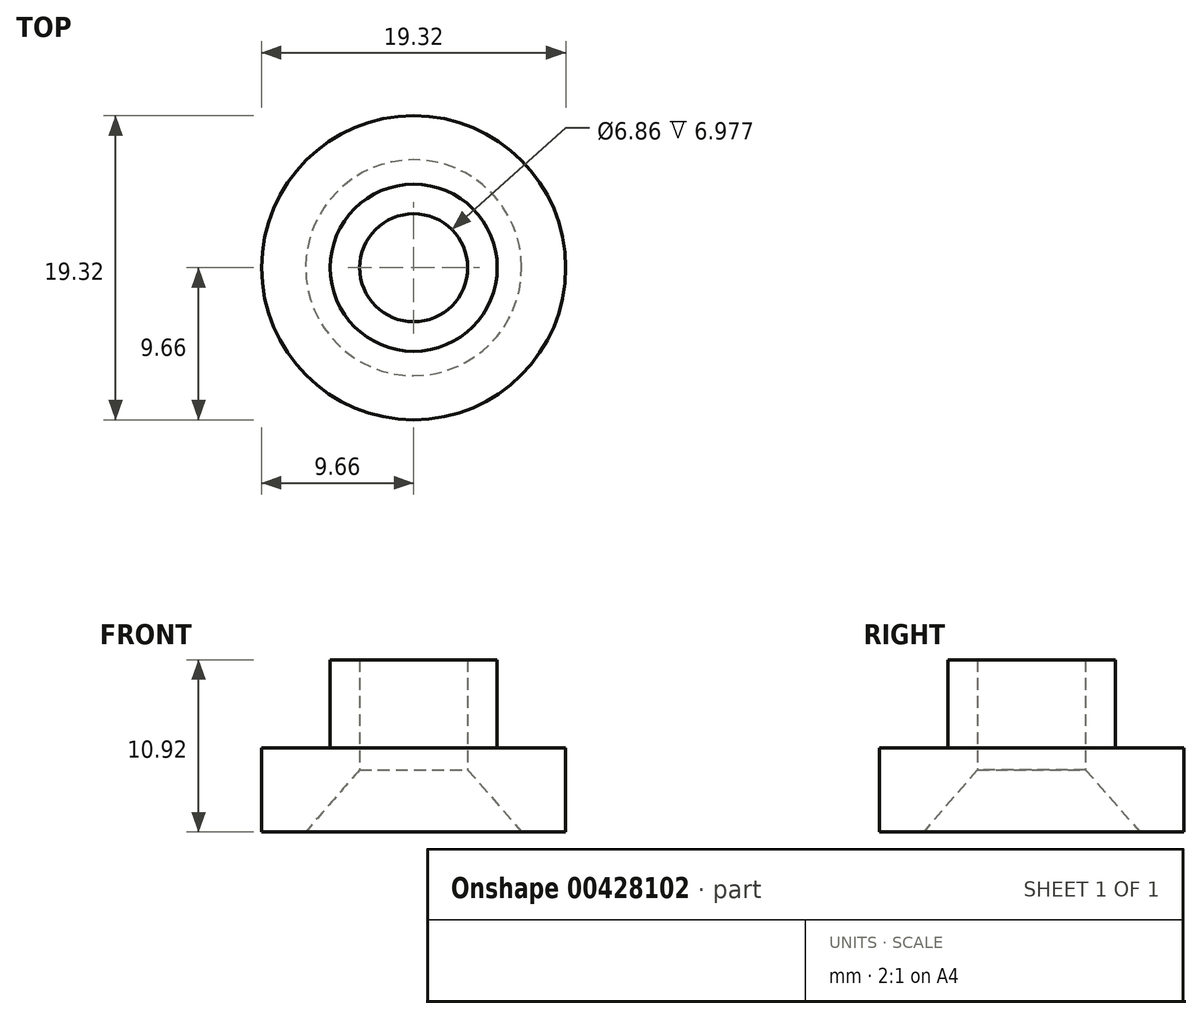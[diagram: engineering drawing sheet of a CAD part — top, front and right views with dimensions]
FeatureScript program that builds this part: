
annotation { "Feature Type Name" : "Feature", "Feature Type Description" : "" }
export const myFeature = defineFeature(function(context is Context, id is Id, definition is map)
    precondition{}
    {
        {
            var Q0;
            Q0=qCreatedBy(makeId("Top.planeOp"),FACE);
            var sketch = newSketch(context, id + "F0", { "sketchPlane" : qUnion([Q0])});
            skCircle(sketch, "E0", {"center": v(0, 0) * mm, "radius": 9.66 * mm});
            skSolve(sketch);
        }
        {
            var Q0;
            Q0=makeQuery(id+"F0.imprint","IMPRINT",FACE,{"disambiguationData":[TD([[makeQuery(id+"F0.imprint","IMPRINT",EDGE,{"derivedFrom":sQuery(id+"F0.wireOp",EDGE,"E0")}),1.0]])]});
            var Q1;
            Q1=sQuery(id+"F0.wireOp",EDGE,"E0");
            extrude(context, id + "F1", {"entities" : qUnion([Q0]), "surfaceEntities" : qUnion([Q1]), "depth" : 5.33 * mm});
        }
        {
            var Q0;
            Q0=makeQuery(id+"F1.opExtrude","CAP_FACE",FACE,{"disambiguationData":[OSD([sQuery(id+"F0.wireOp",EDGE,"E0")])],"isStart":false});
            var sketch = newSketch(context, id + "F2", { "sketchPlane" : qUnion([Q0])});
            skCircle(sketch, "E1", {"center": v(0, 0) * mm, "radius": 5.3 * mm});
            skSolve(sketch);
        }
        {
            var Q0;
            Q0 = qSketchRegion(id + "F2", true);
            extrude(context, id + "F3", {"entities" : qUnion([Q0]), "operationType" : NewBodyOperationType.ADD, "depth" : 5.6 * mm});
        }
        {
            var Q0;
            Q0=makeQuery(id+"F1.opExtrude","CAP_FACE",FACE,{"disambiguationData":[OSD([sQuery(id+"F0.wireOp",EDGE,"E0")])],"isStart":true});
            var sketch = newSketch(context, id + "F4", { "sketchPlane" : qUnion([Q0])});
            skPoint(sketch, "E2", {"position": v(0, 0) * mm});
            skSolve(sketch);
        }
        {
            var Q0;
            Q0=sQuery(id+"F4.wireOp",VERTEX,"E2");
            var Q1;
            Q1=makeQuery(id+"F1.opExtrude","SWEPT_BODY",BODY,{"disambiguationData":[OSD([sQuery(id+"F0.wireOp",EDGE,"E0")])]});
            hole(context, id + "F5", {"style" : HoleStyle.C_SINK, "endStyle" : HoleEndStyle.THROUGH, "holeDiameter" : 6.86 * mm, "cSinkDiameter" : 13.72 * mm, "cSinkAngle" : 82 * degree, "isTappedThrough" : true, "tappedDepth" : 12.7 * mm, "tapClearance" : 3, "startFromSketch" : true, "locations" : qUnion([Q0]), "scope" : qUnion([Q1])});
        }
    });
